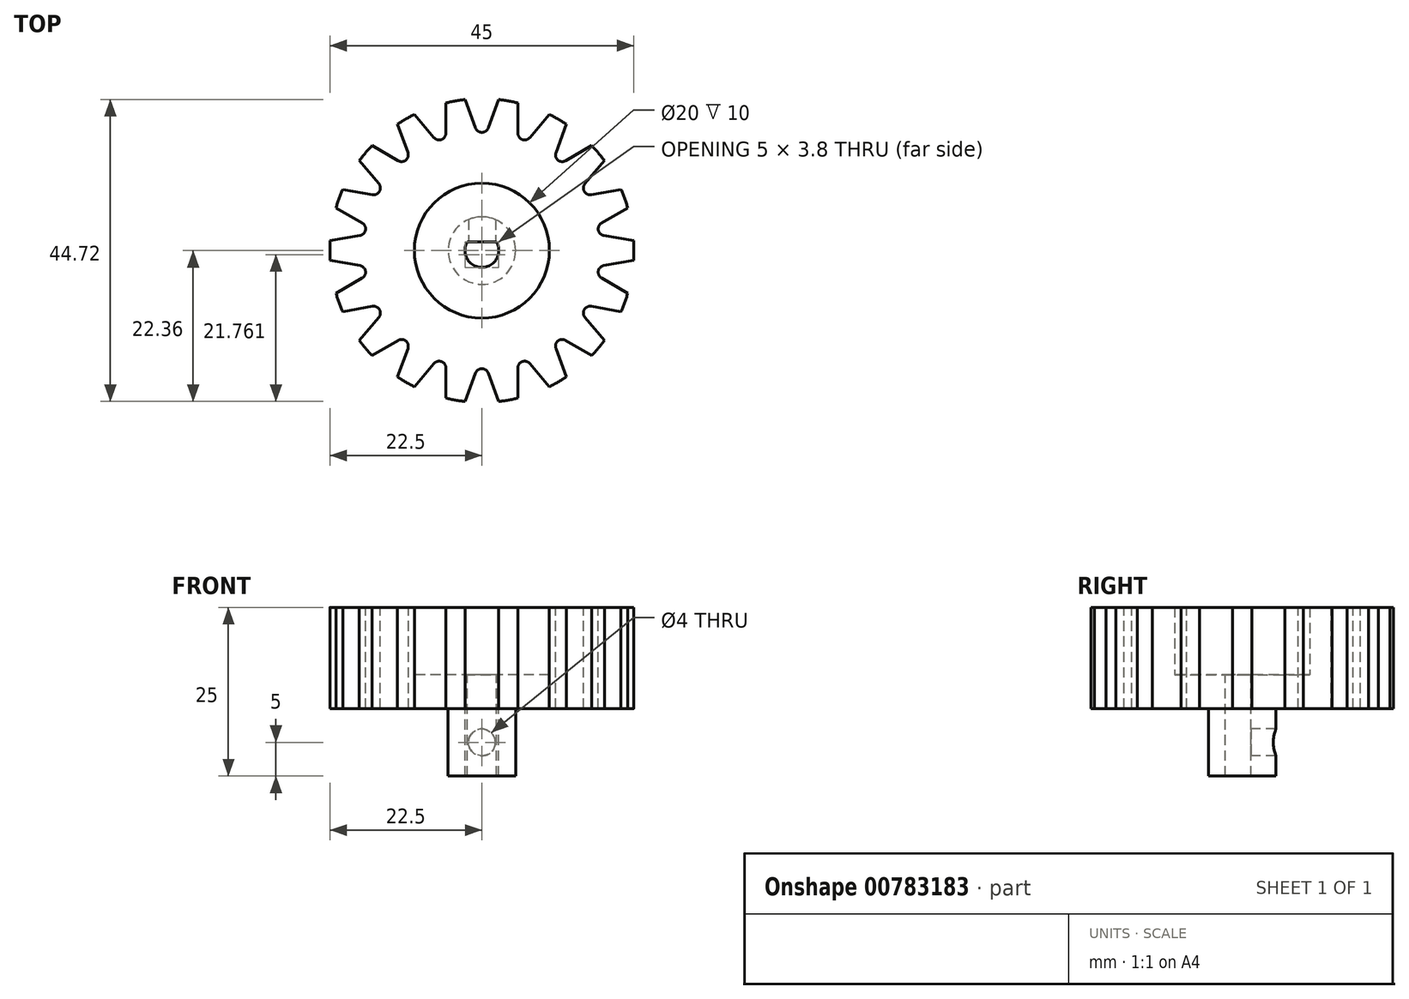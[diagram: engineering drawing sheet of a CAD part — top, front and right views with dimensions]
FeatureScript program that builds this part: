
annotation { "Feature Type Name" : "Feature", "Feature Type Description" : "" }
export const myFeature = defineFeature(function(context is Context, id is Id, definition is map)
    precondition{}
    {
        {
            var Q0;
            Q0=qCreatedBy(makeId("Top.planeOp"),FACE);
            var sketch = newSketch(context, id + "F0", { "sketchPlane" : qUnion([Q0])});
            skCircle(sketch, "E0", {"center": v(0, 0) * mm, "radius": 22.5 * mm});
            skCircle(sketch, "E1", {"center": v(0, 0) * mm, "radius": 2.5 * mm});
            skCircle(sketch, "E2", {"center": v(0, 0) * mm, "radius": 10 * mm});
            skLineSegment(sketch, "E3", {"start": v(2.13, 1.3) * mm, "end": v(-2.13, 1.3) * mm});
            skCircle(sketch, "E4", {"center": v(0, 0) * mm, "radius": 5 * mm});
            skCircle(sketch, "E5", {"center": v(0, 0) * mm, "radius": 17.5 * mm});
            skSolve(sketch);
        }
        {
            var Q0;
            Q0=makeQuery(id+"F0.imprint","IMPRINT",FACE,{"disambiguationData":[TD([[makeQuery(id+"F0.imprint","IMPRINT",EDGE,{"derivedFrom":sQuery(id+"F0.wireOp",EDGE,"E2")}),1.0]])]});
            var Q1;
            Q1=makeQuery(id+"F0.imprint","IMPRINT",FACE,{"disambiguationData":[TD([[makeQuery(id+"F0.imprint","IMPRINT",EDGE,{"derivedFrom":sQuery(id+"F0.wireOp",EDGE,"E4")}),-1.0]])]});
            extrude(context, id + "F1", {"entities" : qUnion([Q0, Q1]), "oppositeDirection" : true, "depth" : 5 * mm, "offsetDistance" : 25 * mm});
        }
        {
            var Q0;
            Q0=makeQuery(id+"F0.imprint","IMPRINT",FACE,{"disambiguationData":[TD([[makeQuery(id+"F0.imprint","IMPRINT",EDGE,{"derivedFrom":sQuery(id+"F0.wireOp",EDGE,"E4")}),1.0]])]});
            var Q1;
            {var subQ0=sQuery(id+"F0.wireOp",EDGE,"E3");Q1=makeQuery(id+"F0.imprint","IMPRINT",FACE,{"disambiguationData":[TD([[makeQuery(id+"F0.imprint","IMPRINT",EDGE,{"derivedFrom":subQ0}),-1.0]])]});}
            extrude(context, id + "F2", {"entities" : qUnion([Q0, Q1]), "operationType" : NewBodyOperationType.ADD, "oppositeDirection" : true, "depth" : 15 * mm, "offsetDistance" : 25 * mm});
        }
        {
            var Q0;
            Q0=makeQuery(id+"F2.opExtrude","SWEPT_FACE",FACE,{"disambiguationData":[OSD([sQuery(id+"F0.wireOp",EDGE,"E3")])]});
            var sketch = newSketch(context, id + "F3", { "sketchPlane" : qUnion([Q0])});
            skCircle(sketch, "E6", {"center": v(0, -10) * mm, "radius": 2 * mm});
            skSolve(sketch);
        }
        {
            var Q0;
            Q0=qSketchRegion(id+"F3",true);
            extrude(context, id + "F4", {"entities" : qUnion([Q0]), "operationType" : NewBodyOperationType.REMOVE, "endBound" : BoundingType.THROUGH_ALL, "oppositeDirection" : true, "depth" : 25 * mm, "offsetDistance" : 25 * mm});
        }
        {
            var Q0;
            Q0=makeQuery(id+"F0.imprint","IMPRINT",FACE,{"disambiguationData":[TD([[makeQuery(id+"F0.imprint","IMPRINT",EDGE,{"derivedFrom":sQuery(id+"F0.wireOp",EDGE,"E2")}),-1.0]])]});
            var Q1;
            Q1=makeQuery(id+"F0.imprint","IMPRINT",FACE,{"disambiguationData":[TD([[makeQuery(id+"F0.imprint","IMPRINT",EDGE,{"derivedFrom":sQuery(id+"F0.wireOp",EDGE,"E0")}),1.0]])]});
            extrude(context, id + "F5", {"entities" : qUnion([Q0, Q1]), "operationType" : NewBodyOperationType.ADD, "oppositeDirection" : true, "depth" : 5 * mm, "offsetDistance" : 25 * mm});
        }
        {
            var Q0;
            Q0=makeQuery(id+"F0.imprint","IMPRINT",FACE,{"disambiguationData":[TD([[makeQuery(id+"F0.imprint","IMPRINT",EDGE,{"derivedFrom":sQuery(id+"F0.wireOp",EDGE,"E0")}),1.0]])]});
            var Q1;
            Q1=makeQuery(id+"F0.imprint","IMPRINT",FACE,{"disambiguationData":[TD([[makeQuery(id+"F0.imprint","IMPRINT",EDGE,{"derivedFrom":sQuery(id+"F0.wireOp",EDGE,"E2")}),-1.0]])]});
            extrude(context, id + "F6", {"entities" : qUnion([Q0, Q1]), "operationType" : NewBodyOperationType.ADD, "depth" : 10 * mm, "offsetDistance" : 25 * mm});
        }
        {
            var Q0;
            Q0=makeQuery(id+"F6.opExtrude","CAP_FACE",FACE,{"disambiguationData":[OSD([sQuery(id+"F0.wireOp",EDGE,"E0"),sQuery(id+"F0.wireOp",EDGE,"E2")])],"isStart":false});
            var sketch = newSketch(context, id + "F7", { "sketchPlane" : qUnion([Q0])});
            skPoint(sketch, "E7.orphan", {"position": v(0, 0) * mm});
            skLineSegment(sketch, "E8", {"start": v(2.47, 22.36) * mm, "end": v(0.94, 18.16) * mm});
            skLineSegment(sketch, "E9", {"start": v(0, 17.5) * mm, "end": v(0, 17.5) * mm});
            skPoint(sketch, "E10.visualSharp", {"position": v(0.7, 17.5) * mm});
            skArc(sketch, "E10.filletArc", {"start": v(0, 17.5) * mm, "mid": v(0.57, 17.68) * mm, "end": v(0.94, 18.16) * mm});
            skLineSegment(sketch, "E11.MirrorCS", {"start": v(-2.47, 22.36) * mm, "end": v(-0.94, 18.16) * mm});
            skArc(sketch, "E12.MirrorCS", {"start": v(0, 17.5) * mm, "mid": v(-0.57, 17.68) * mm, "end": v(-0.94, 18.16) * mm});
            skSolve(sketch);
        }
        {
            var Q0;
            {var subQ1=sQuery(id+"F7.wireOp",EDGE,"E8");Q0=makeQuery(id+"F7.imprint","IMPRINT",FACE,{"disambiguationData":[TD([[makeQuery(id+"F7.imprint","IMPRINT",EDGE,{"derivedFrom":subQ1}),-1.0]])]});}
            extrude(context, id + "F8", {"entities" : qUnion([Q0]), "operationType" : NewBodyOperationType.REMOVE, "endBound" : BoundingType.THROUGH_ALL, "oppositeDirection" : true, "depth" : 25 * mm, "offsetDistance" : 25 * mm});
        }
        {
            var Q0;
            Q0=makeQuery(id+"F8.boolean.opBoolean","COPY",FACE,{"derivedFrom":makeQuery(id+"F8.opExtrude","SWEPT_FACE",FACE,{"disambiguationData":[OSD([sQuery(id+"F7.wireOp",EDGE,"E11.MirrorCS")])]})});
            var Q1;
            Q1=makeQuery(id+"F8.boolean.opBoolean","COPY",FACE,{"derivedFrom":makeQuery(id+"F8.opExtrude","SWEPT_FACE",FACE,{"disambiguationData":[OSD([sQuery(id+"F7.wireOp",EDGE,"E12.MirrorCS")])]})});
            var Q2;
            Q2=makeQuery(id+"F8.boolean.opBoolean","COPY",FACE,{"derivedFrom":makeQuery(id+"F8.opExtrude","SWEPT_FACE",FACE,{"disambiguationData":[OSD([sQuery(id+"F7.wireOp",EDGE,"E9"),sQuery(id+"F7.wireOp",EDGE,"E9")])]})});
            var Q3;
            Q3=makeQuery(id+"F8.boolean.opBoolean","COPY",FACE,{"derivedFrom":makeQuery(id+"F8.opExtrude","SWEPT_FACE",FACE,{"disambiguationData":[OSD([sQuery(id+"F7.wireOp",EDGE,"E10.filletArc")])]})});
            var Q4;
            Q4=makeQuery(id+"F8.boolean.opBoolean","COPY",FACE,{"derivedFrom":makeQuery(id+"F8.opExtrude","SWEPT_FACE",FACE,{"disambiguationData":[OSD([sQuery(id+"F7.wireOp",EDGE,"E8")])]})});
            var Q5;
            Q5=makeQuery(id+"F2.opExtrude","SWEPT_FACE",FACE,{"disambiguationData":[OSD([sQuery(id+"F0.wireOp",EDGE,"E1")])]});
            circularPattern(context, id + "F9", {"patternType" : PatternType.FACE, "operationType" : NewBodyOperationType.REMOVE, "faces" : qUnion([Q0, Q1, Q2, Q3, Q4]), "axis" : qUnion([Q5]), "angle" : 10 * degree, "instanceCount" : 36, "oppositeDirection" : true});
        }
    });
